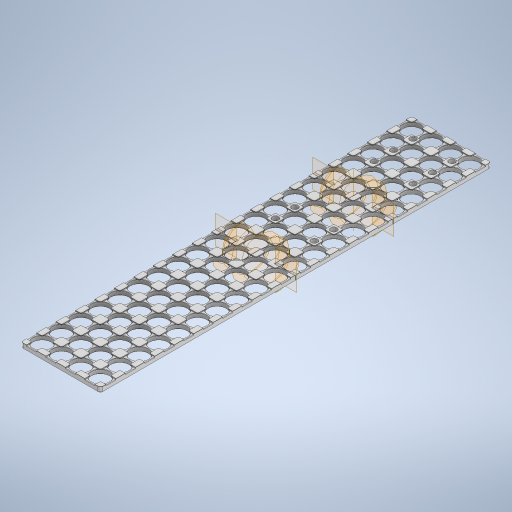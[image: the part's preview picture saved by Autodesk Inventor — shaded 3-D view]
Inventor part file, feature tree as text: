
AUTODESK INVENTOR PART (.ipt)
format: ipt  version: 2024.2 (Build 282272000, 272)  size: 6,434,816 bytes
history: native  units: mm
features: other x22, surface_op x13, chamfer x9, revolve x7, thicken_offset x6, pattern_linear x5, sketch x5, extrude x3, fillet x3, hole x2, split x2, pattern_circular x1
ambient origin geometry x8: Origin, YZ Plane, XZ Plane, XY Plane, X Axis, Y Axis, Z Axis, Center Point
bodies: Solid1 (feature_tree), Solid2 (feature_tree), Solid4 (feature_tree)
feature tree (78):
  extrude  "Extrusion1"  Depth=23.5mm
  extrude  "Extrusion2"  Depth=5.75mm TaperAngle=0.0deg
  fillet  "Fillet1"  Radius=5.75mm
  chamfer  "Chamfer1"  Distance=1.0mm
  chamfer  "Chamfer2"  Distance=0.4mm Angle=45.0deg
  pattern_linear  "Rectangular Pattern1"  Count1=4 Spacing1=23.5mm
  sketch  "Sketch3"  dims[d6=5.75mm d7=1.0mm d8=0.0mm]
  surface_op  "Stitch Surface1"
  other  "Work Axis1"
  pattern_circular  "Circular Pattern1"  Count=20  [1 undecoded]
  surface_op  "Extend3"
  surface_op  "Extend4"
  surface_op  "Stitch Surface8"
  pattern_linear  "Rectangular Pattern2"  Spacing1=23.5mm  [1 undecoded]
  hole  "Hole1"  [1 undecoded]
  chamfer  "Chamfer3"  Distance=23.5mm
  hole  "Hole2"  [1 undecoded]
  chamfer  "Chamfer4"  Distance=13.0mm
  pattern_linear  "Rectangular Pattern4"  Count1=2 Spacing1=23.5mm
  pattern_linear  "Rectangular Pattern5"  Spacing1=10.0mm  [1 undecoded]
  chamfer  "Chamfer5"  Distance=23.5mm
  chamfer  "Chamfer6"  Angle=180.0deg  [1 undecoded]
  thicken_offset  "Thicken8"
  fillet  "Fillet2"  [1 undecoded]
  chamfer  "Chamfer7"  Angle=180.0deg  [1 undecoded]
  chamfer  "Chamfer8"  Angle=180.0deg  [1 undecoded]
  chamfer  "Chamfer9"  Angle=90.0deg  [1 undecoded]
  split  "Split1"
  thicken_offset  "Thicken3"
  thicken_offset  "Thicken4"
  pattern_linear  "Rectangular Pattern6"  Spacing1=90.0deg  [1 undecoded]
  surface_op  "Stitch Surface11"
  split  "Split2"
  thicken_offset  "Thicken5"
  thicken_offset  "Thicken6"
  thicken_offset  "Thicken7"
  fillet  "Fillet3"  [1 undecoded]
  sketch  "Sketch1"  dims[d0=23.5mm d1=23.5mm]
  sketch  "Sketch2"  dims[d2=21.7mm d3=5.0mm d4=0.0mm d5=5.75mm]
  other  "Srf1"
  other  "Srf2"
  other  "Srf3"
  other  "Srf4"
  other  "Srf5"
  other  "Srf6"
  other  "Srf7"
  other  "Srf8"
  other  "Srf9"
  other  "Srf10"
  other  "Srf11"
  other  "Srf12"
  other  "Srf14"
  other  "Srf13"
  other  "Srf15"
  other  "Srf17"
  sketch  "Sketch4"  dims[d9=2.0mm d10=0.4mm d11=2.0mm d12=45.0deg]
  sketch  "Sketch5"  dims[d13=0.2mm d14=2.0mm d15=45.0deg d16=40.0mm d18=23.5mm d19=200.0mm d21=23.5mm d22=23.5mm d23=23.5mm d27=23.5mm d29=45.0deg d30=13.0mm d31=20.0mm d33=23.5mm d34=10.0mm d36=23.5mm d39=23.5mm d41=180.0deg d42=90.0deg d43=180.0deg d44=180.0deg d45=90.0deg d46=90.0deg d47=90.0deg d48=34.0mm d49=0.0mm d50=20.0mm d51=360.0deg d59=30.0mm d61=117.5mm d64=6.756mm d65=6.0mm d66=12.878mm d67=2.0mm d68=14.3117mm d69=8.0mm d70=0.0mm d71=0.5mm d72=2.0mm d73=45.0deg d80=6.756mm d81=6.0mm d82=4.0mm d83=2.0mm d84=90.0deg d85=8.0mm d86=0.0mm d87=0.5mm d88=2.0mm d89=45.0deg d90=20.0mm d92=47.0mm d93=20.0mm d95=23.5mm d96=30.0mm d98=23.5mm d99=20.0mm d101=47.0mm d102=0.5mm d103=2.0mm d104=45.0deg d105=0.5mm d106=2.0mm d107=45.0deg d108=0.3mm d109=0.3mm d110=0.3mm d111=0.3mm d112=20.0mm d114=117.5mm d115=0.3mm d116=0.3mm d117=0.3mm d118=0.3mm d119=0.3mm d120=0.3mm d121=1.0mm d122=1.0mm d123=2.0mm d124=2.0mm d125=0.5mm d126=2.0mm d127=45.0deg d128=0.2mm d129=2.0mm d130=45.0deg d131=0.5mm d132=2.0mm d133=45.0deg d134=3.0mm d135=1.25mm]
  other  "Srf18"
  other  "Srf19"
  other  "Srf20"
  revolve  "RevolutionSrf1"  [1 undecoded]
  revolve  "RevolutionSrf2"  [1 undecoded]
  revolve  "RevolutionSrf3"  Angle=360.0deg
  revolve  "RevolutionSrf4"  [1 undecoded]
  revolve  "RevolutionSrf5"  Angle=45.0deg
  revolve  "RevolutionSrf6"  Angle=45.0deg
  revolve  "RevolutionSrf7"  [1 undecoded]
  extrude  "ExtrusionSrf1"  Depth=23.5mm
  surface_op  "Stitch Surface2"
  surface_op  "Stitch Surface3"
  surface_op  "Stitch Surface4"
  surface_op  "Stitch Surface5"
  surface_op  "Stitch Surface6"
  other  "End"
  surface_op  "Stitch Surface9"
  surface_op  "Stitch Surface10"
  other  "Middle"
  surface_op  "Boundary Patch1"
note: 16 required parameter values undecoded (feature->parameter linkage not recoverable at this tier; creation-order binding heuristic only, values carry confidence <= 0.55)